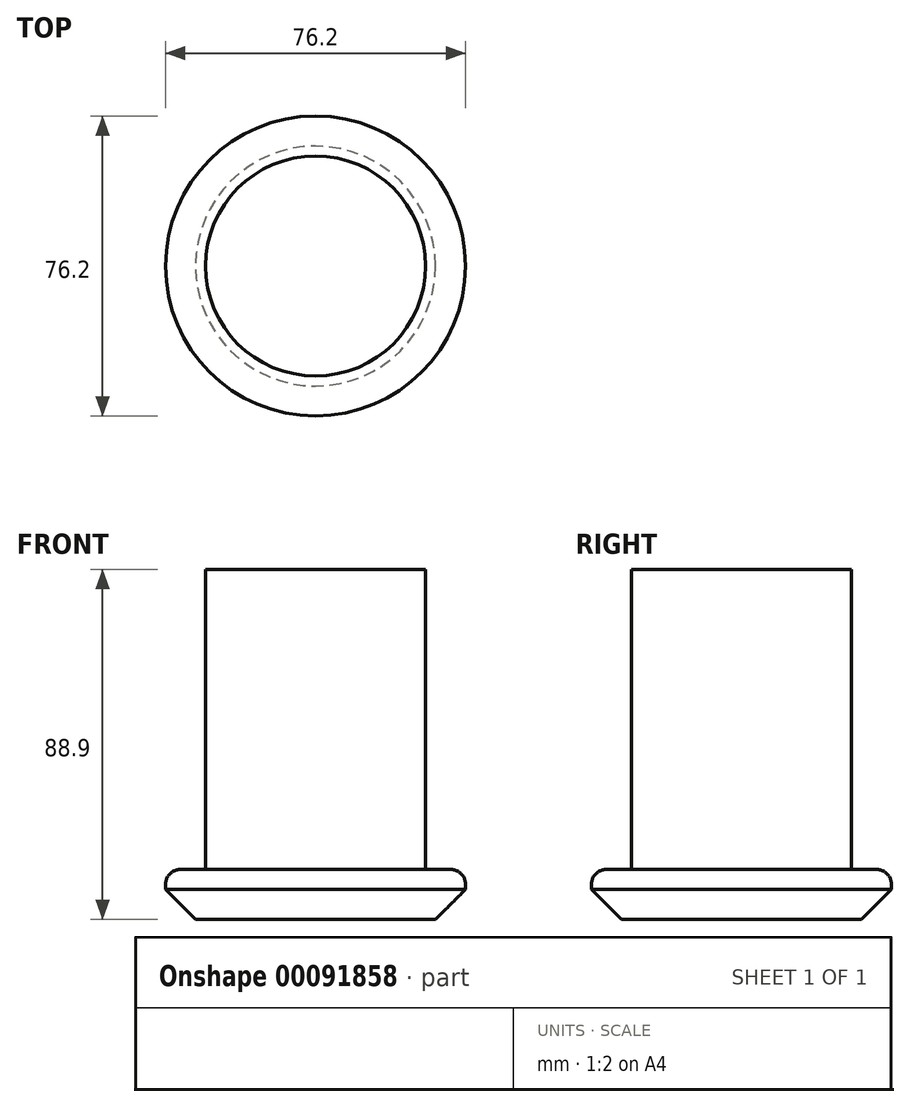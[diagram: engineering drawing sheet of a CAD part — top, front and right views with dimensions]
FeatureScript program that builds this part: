
annotation { "Feature Type Name" : "Feature", "Feature Type Description" : "" }
export const myFeature = defineFeature(function(context is Context, id is Id, definition is map)
    precondition{}
    {
        {
            var Q0;
            Q0=qCreatedBy(makeId("Top.planeOp"),FACE);
            var sketch = newSketch(context, id + "F0", { "sketchPlane" : qUnion([Q0])});
            skCircle(sketch, "E0", {"center": v(0, 0) * mm, "radius": 38.1 * mm});
            skSolve(sketch);
        }
        {
            var Q0;
            Q0=makeQuery(id+"F0.imprint","IMPRINT",FACE,{"disambiguationData":[TD([[makeQuery(id+"F0.imprint","IMPRINT",EDGE,{"derivedFrom":sQuery(id+"F0.wireOp",EDGE,"E0")}),1.0]])]});
            extrude(context, id + "F1", {"entities" : qUnion([Q0]), "depth" : 12.7 * mm});
        }
        {
            var Q0;
            Q0=makeQuery(id+"F1.opExtrude","CAP_EDGE",EDGE,{"disambiguationData":[OSD([sQuery(id+"F0.wireOp",EDGE,"E0")])],"isStart":false});
            fillet(context, id + "F2", {"entities" : qUnion([Q0]), "radius" : 3.8 * mm, "tangentPropagation" : true, "allowEdgeOverflow" : false});
        }
        {
            var Q0;
            Q0=makeQuery(id+"F1.opExtrude","CAP_EDGE",EDGE,{"disambiguationData":[OSD([sQuery(id+"F0.wireOp",EDGE,"E0")])],"isStart":true});
            chamfer(context, id + "F3", {"entities" : qUnion([Q0]), "width" : 7.62 * mm, "tangentPropagation" : true});
        }
        {
            var Q0;
            Q0=makeQuery(id+"F1.opExtrude","CAP_FACE",FACE,{"disambiguationData":[OSD([sQuery(id+"F0.wireOp",EDGE,"E0")])],"isStart":false});
            var sketch = newSketch(context, id + "F4", { "sketchPlane" : qUnion([Q0])});
            skCircle(sketch, "E1", {"center": v(0, 0) * mm, "radius": 27.94 * mm});
            skSolve(sketch);
        }
        {
            var Q0;
            Q0=makeQuery(id+"F4.imprint","IMPRINT",FACE,{"disambiguationData":[TD([[makeQuery(id+"F4.imprint","IMPRINT",EDGE,{"derivedFrom":sQuery(id+"F4.wireOp",EDGE,"E1")}),1.0]])]});
            extrude(context, id + "F5", {"entities" : qUnion([Q0]), "operationType" : NewBodyOperationType.ADD, "depth" : 76.2 * mm});
        }
    });
